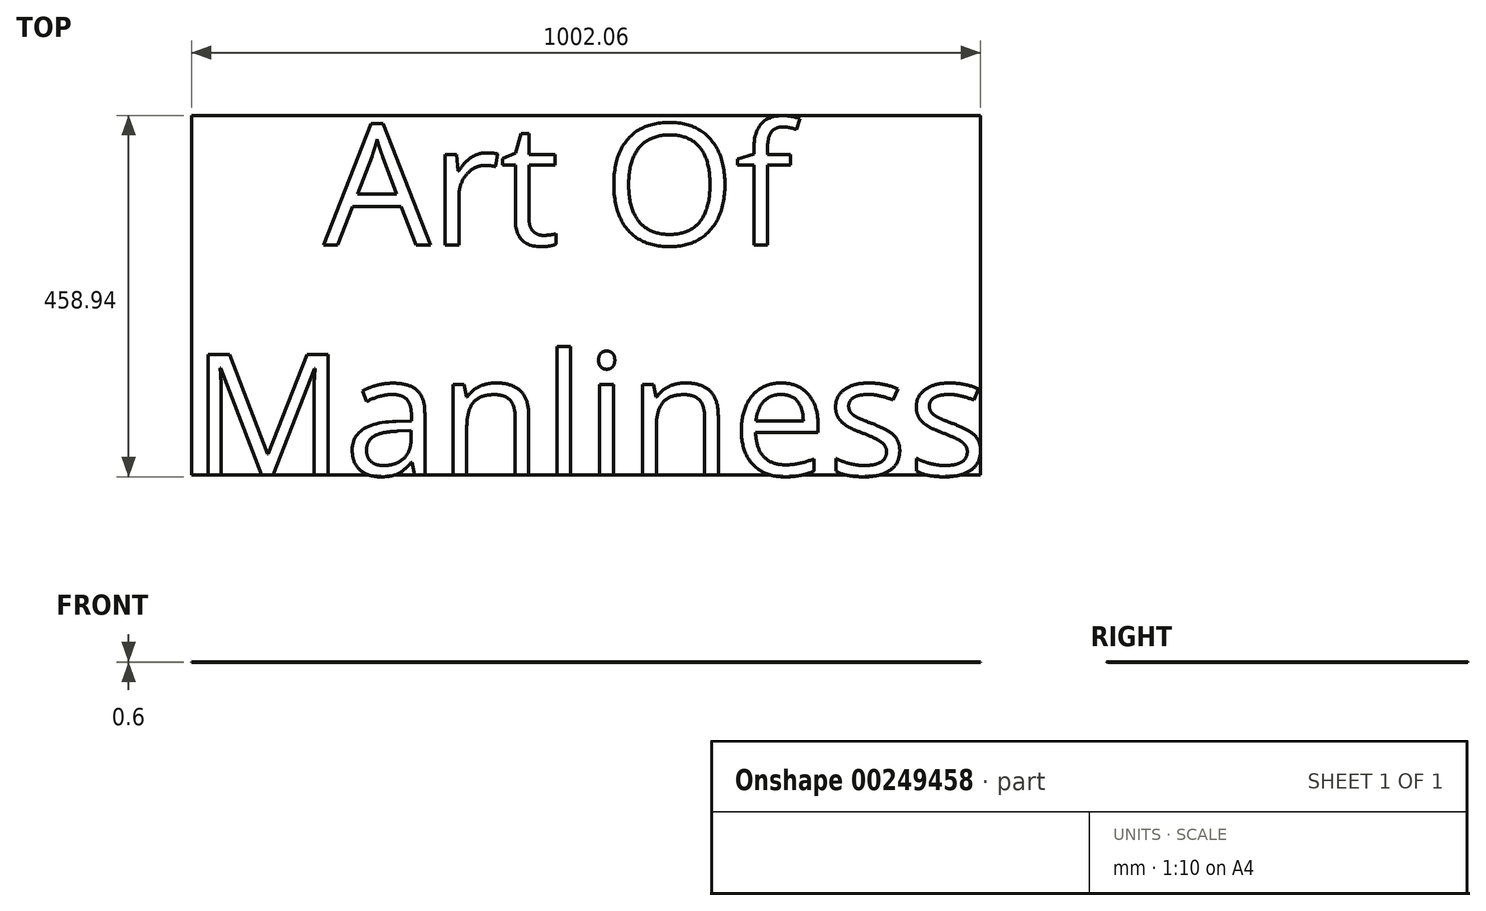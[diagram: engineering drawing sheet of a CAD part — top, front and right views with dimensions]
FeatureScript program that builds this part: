
annotation { "Feature Type Name" : "Feature", "Feature Type Description" : "" }
export const myFeature = defineFeature(function(context is Context, id is Id, definition is map)
    precondition{}
    {
        {
            var Q0;
            Q0=qCreatedBy(makeId("Top.planeOp"),FACE);
            var sketch = newSketch(context, id + "F0", { "sketchPlane" : qUnion([Q0])});
            skText(sketch, "E0", { "text": "   Art Of \nManliness", "fontName": "OpenSans-Regular.ttf"});
            const initialGuessF0  = {"E0": [0, 0, 1, 0, 0.15477]};
            skSetInitialGuess(sketch, initialGuessF0);
            skSolve(sketch);
        }
        {
            var Q0;
            Q0 = qSketchRegion(id + "F0", true);
            extrude(context, id + "F1", {"entities" : qUnion([Q0]), "depth" : 0.3 * mm});
        }
        {
            var Q0;
            Q0=qCreatedBy(makeId("Top.planeOp"),FACE);
            var sketch = newSketch(context, id + "F2", { "sketchPlane" : qUnion([Q0])});
            skLineSegment(sketch, "E1.top", {"start": v(0, 0) * mm, "end": v(0, 0) * mm});
            skLineSegment(sketch, "E2.bottom", {"start": v(0, 164.48) * mm, "end": v(1002.06, 164.48) * mm});
            skLineSegment(sketch, "E2.top", {"start": v(0, -292.35) * mm, "end": v(1002.06, -292.35) * mm});
            skLineSegment(sketch, "E2.left", {"start": v(0, 164.48) * mm, "end": v(0, -292.35) * mm});
            skLineSegment(sketch, "E2.right", {"start": v(1002.06, 164.48) * mm, "end": v(1002.06, -292.35) * mm});
            skSolve(sketch);
        }
        {
            var Q0;
            Q0 = qSketchRegion(id + "F2", true);
            extrude(context, id + "F3", {"entities" : qUnion([Q0]), "operationType" : NewBodyOperationType.ADD, "oppositeDirection" : true, "depth" : 0.3 * mm});
        }
    });
